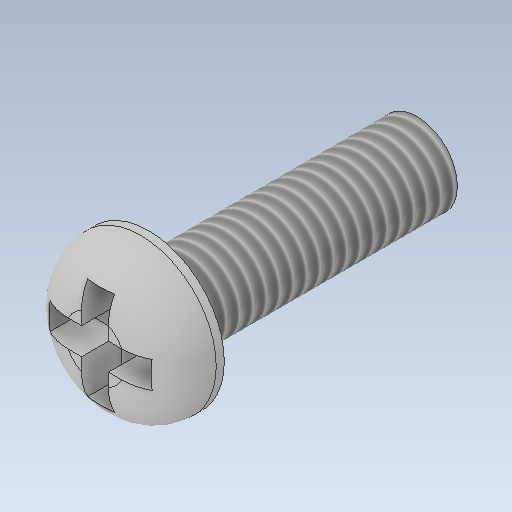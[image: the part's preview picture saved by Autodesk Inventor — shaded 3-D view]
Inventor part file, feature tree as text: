
AUTODESK INVENTOR PART (.ipt)
format: ipt  version: 2020 (Build 240168000, 168)  size: 190,976 bytes
history: native  units: mm
features: extrude x3, sketch x3, other x1, fillet x1, thread x1
ambient origin geometry x8: Origin, YZ Plane, XZ Plane, XY Plane, X Axis, Y Axis, Z Axis, Center Point
bodies: Body1 (feature_tree)
feature tree (9):
  other  "Твердое тело1"
  extrude  "Выдавливание1"  Depth=10.0mm TaperAngle=0.0deg
  extrude  "Выдавливание2"  Depth=2.0mm TaperAngle=0.0deg
  fillet  "Сопряжение1"  Radius=1.7mm
  extrude  "Выдавливание3"  Depth=1.5mm TaperAngle=0.0deg
  thread  "Резьба1"
  sketch  "Эскиз1"
  sketch  "Эскиз2"
  sketch  "Эскиз3"
